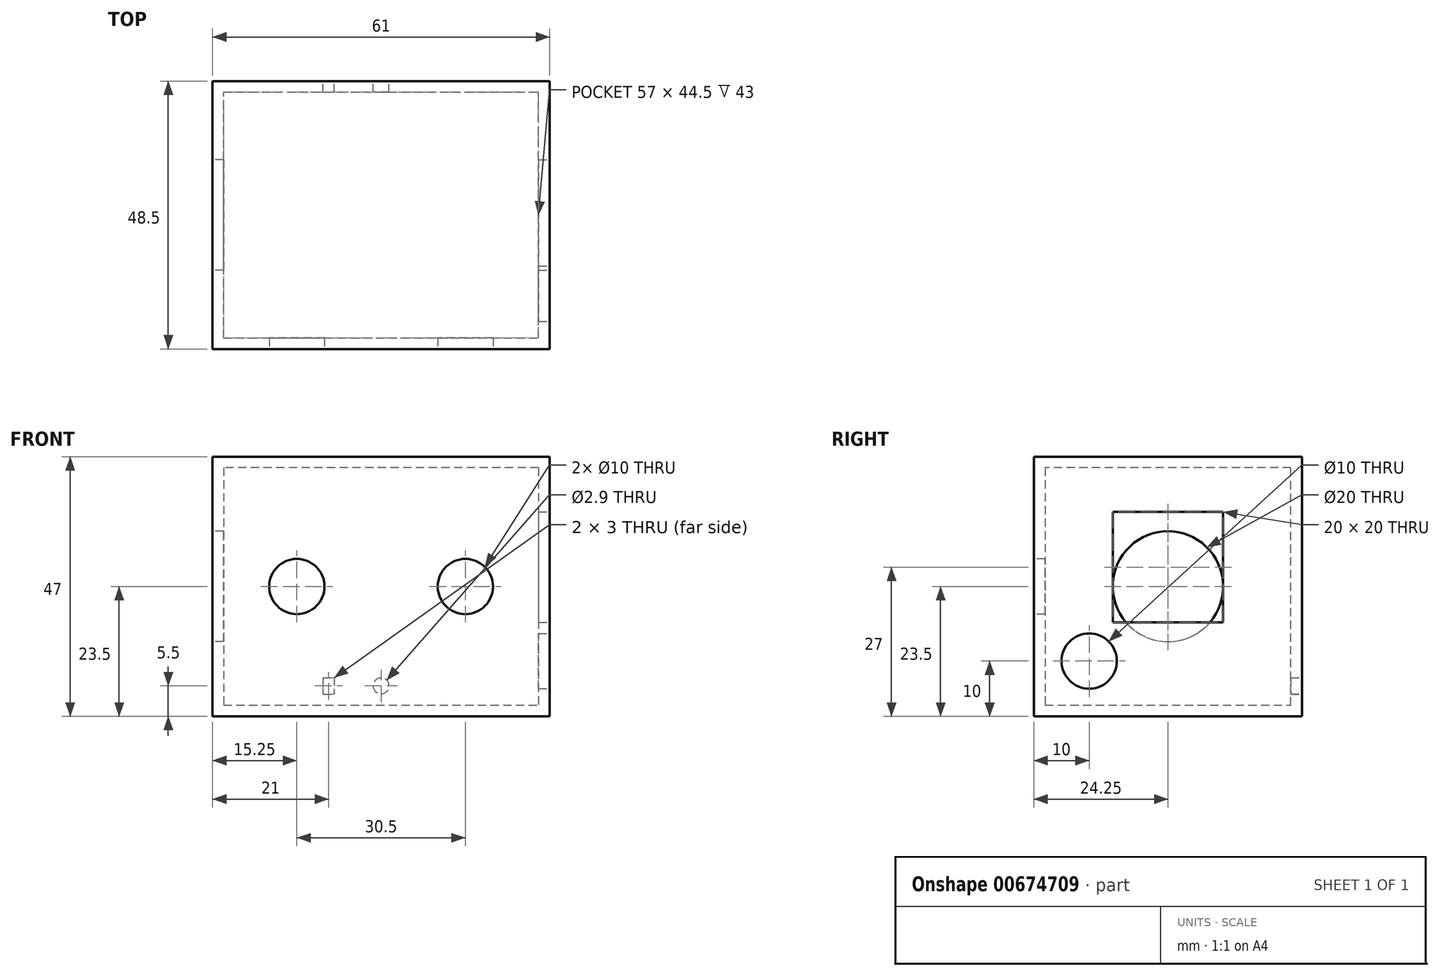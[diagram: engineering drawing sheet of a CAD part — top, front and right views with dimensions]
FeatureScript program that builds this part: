
annotation { "Feature Type Name" : "Feature", "Feature Type Description" : "" }
export const myFeature = defineFeature(function(context is Context, id is Id, definition is map)
    precondition{}
    {
        {
            var Q0;
            Q0=qCreatedBy(makeId("Front.planeOp"),FACE);
            var sketch = newSketch(context, id + "F0", { "sketchPlane" : qUnion([Q0])});
            skLineSegment(sketch, "E0", {"start": v(0, 47) * mm, "end": v(61, 47) * mm});
            skLineSegment(sketch, "E1", {"start": v(61, 47) * mm, "end": v(61, 0) * mm});
            skLineSegment(sketch, "E2", {"start": v(61, 0) * mm, "end": v(0, 0) * mm});
            skLineSegment(sketch, "E3", {"start": v(0, 0) * mm, "end": v(0, 47) * mm});
            skCircle(sketch, "E4", {"center": v(30.5, 5.5) * mm, "radius": 1.45 * mm});
            skLineSegment(sketch, "E5", {"start": v(20, 7) * mm, "end": v(20, 4) * mm});
            skLineSegment(sketch, "E6", {"start": v(20, 5.5) * mm, "end": v(20, 7) * mm});
            skLineSegment(sketch, "E7", {"start": v(20, 7) * mm, "end": v(22, 7) * mm});
            skLineSegment(sketch, "E8", {"start": v(22, 7) * mm, "end": v(22, 5.5) * mm});
            skLineSegment(sketch, "E9.MirrorCS", {"start": v(22, 4) * mm, "end": v(22, 5.5) * mm});
            skLineSegment(sketch, "E10.MirrorCS", {"start": v(20, 4) * mm, "end": v(22, 4) * mm});
            skLineSegment(sketch, "E11.MirrorCS", {"start": v(20, 5.5) * mm, "end": v(20, 4) * mm});
            skPoint(sketch, "E12.start.orphan", {"position": v(30.5, 0) * mm});
            skPoint(sketch, "E13.trimOffspring.end.orphan", {"position": v(30.5, 47) * mm});
            skPoint(sketch, "E13.trimOffspring.start.orphan", {"position": v(30.5, 23.5) * mm});
            skSolve(sketch);
        }
        {
            var Q0;
            Q0=makeQuery(id+"F0.imprint","IMPRINT",FACE,{"disambiguationData":[TD([[makeQuery(id+"F0.imprint","IMPRINT",EDGE,{"derivedFrom":sQuery(id+"F0.wireOp",EDGE,"E0")}),-1.0]])]});
            extrude(context, id + "F1", {"entities" : qUnion([Q0]), "depth" : 2 * mm, "offsetDistance" : 25 * mm});
        }
        {
            var Q0;
            Q0=makeQuery(id+"F1.opExtrude","SWEPT_FACE",FACE,{"disambiguationData":[OSD([sQuery(id+"F0.wireOp",EDGE,"E1")])]});
            cPlane(context, id + "F2", {"entities" : qUnion([Q0]), "cplaneType" : CPlaneType.OFFSET, "offset" : 0 * mm, "width" : 150 * mm, "height" : 150 * mm});
        }
        {
            var Q0;
            Q0=qCreatedBy(id+"F2.planeOp",FACE);
            var sketch = newSketch(context, id + "F3", { "sketchPlane" : qUnion([Q0])});
            skLineSegment(sketch, "E14", {"start": v(0, 0) * mm, "end": v(0, 47) * mm});
            skLineSegment(sketch, "E15", {"start": v(0, 47) * mm, "end": v(-48.5, 47) * mm});
            skLineSegment(sketch, "E16", {"start": v(-48.5, 47) * mm, "end": v(-48.5, 0) * mm});
            skLineSegment(sketch, "E17", {"start": v(-48.5, 0) * mm, "end": v(0, 0) * mm});
            skPoint(sketch, "E18.endSnap0", {"position": v(-48.5, 23.5) * mm});
            skPoint(sketch, "E18.start.orphan", {"position": v(-24.25, 47) * mm});
            skPoint(sketch, "E19.orphan", {"position": v(-36.38, 23.5) * mm});
            skPoint(sketch, "E20.end.orphan", {"position": v(-38.5, 0) * mm});
            skLineSegment(sketch, "E21.top", {"start": v(-24.25, 37) * mm, "end": v(-14.25, 37) * mm});
            skLineSegment(sketch, "E22.top", {"start": v(-24.25, 37) * mm, "end": v(-34.25, 37) * mm});
            skLineSegment(sketch, "E23", {"start": v(-34.25, 37) * mm, "end": v(-34.25, 17) * mm});
            skLineSegment(sketch, "E24", {"start": v(-34.25, 17) * mm, "end": v(-14.25, 17) * mm});
            skLineSegment(sketch, "E25", {"start": v(-14.25, 17) * mm, "end": v(-14.25, 37) * mm});
            skPoint(sketch, "E26", {"position": v(-48.5, 10) * mm});
            skCircle(sketch, "E27", {"center": v(-38.5, 10) * mm, "radius": 5 * mm});
            skSolve(sketch);
        }
        {
            var Q0;
            Q0=makeQuery(id+"F3.imprint","IMPRINT",FACE,{"disambiguationData":[TD([[makeQuery(id+"F3.imprint","IMPRINT",EDGE,{"derivedFrom":sQuery(id+"F3.wireOp",EDGE,"E14")}),1.0]])]});
            extrude(context, id + "F4", {"entities" : qUnion([Q0]), "operationType" : NewBodyOperationType.ADD, "oppositeDirection" : true, "depth" : 2 * mm, "offsetDistance" : 25 * mm});
        }
        {
            var Q0;
            Q0=qCreatedBy(makeId("Right.planeOp"),FACE);
            var sketch = newSketch(context, id + "F5", { "sketchPlane" : qUnion([Q0])});
            skLineSegment(sketch, "E28", {"start": v(0, 0) * mm, "end": v(0, 47) * mm});
            skLineSegment(sketch, "E29", {"start": v(0, 47) * mm, "end": v(-48.5, 47) * mm});
            skLineSegment(sketch, "E30", {"start": v(-48.5, 47) * mm, "end": v(-48.5, 0) * mm});
            skLineSegment(sketch, "E31", {"start": v(-48.5, 0) * mm, "end": v(0, 0) * mm});
            skPoint(sketch, "E32.endSnap0", {"position": v(-48.5, 23.5) * mm});
            skCircle(sketch, "E33", {"center": v(-24.25, 23.5) * mm, "radius": 10 * mm});
            skPoint(sketch, "E34.orphan", {"position": v(-24.25, 47) * mm});
            skSolve(sketch);
        }
        {
            var Q0;
            Q0=makeQuery(id+"F5.imprint","IMPRINT",FACE,{"disambiguationData":[TD([[makeQuery(id+"F5.imprint","IMPRINT",EDGE,{"derivedFrom":sQuery(id+"F5.wireOp",EDGE,"E28")}),1.0]])]});
            extrude(context, id + "F6", {"entities" : qUnion([Q0]), "operationType" : NewBodyOperationType.ADD, "depth" : 2 * mm, "offsetDistance" : 25 * mm});
        }
        {
            var Q0;
            Q0=makeQuery(id+"F4.opExtrude","SWEPT_FACE",FACE,{"disambiguationData":[OSD([sQuery(id+"F3.wireOp",EDGE,"E16")])]});
            cPlane(context, id + "F7", {"entities" : qUnion([Q0]), "cplaneType" : CPlaneType.OFFSET, "offset" : 0 * mm, "width" : 150 * mm, "height" : 150 * mm});
        }
        {
            var Q0;
            Q0=qCreatedBy(id+"F7.planeOp",FACE);
            var sketch = newSketch(context, id + "F8", { "sketchPlane" : qUnion([Q0])});
            skLineSegment(sketch, "E35", {"start": v(0, 0) * mm, "end": v(0, 47) * mm});
            skLineSegment(sketch, "E36", {"start": v(0, 47) * mm, "end": v(61, 47) * mm});
            skLineSegment(sketch, "E37", {"start": v(61, 47) * mm, "end": v(61, 0) * mm});
            skLineSegment(sketch, "E38", {"start": v(61, 0) * mm, "end": v(0, 0) * mm});
            skCircle(sketch, "E39", {"center": v(15.25, 23.5) * mm, "radius": 5 * mm});
            skCircle(sketch, "E40", {"center": v(45.75, 23.5) * mm, "radius": 5 * mm});
            skPoint(sketch, "E41.orphan", {"position": v(30.5, 47) * mm});
            skPoint(sketch, "E42.end.orphan", {"position": v(0, 23.5) * mm});
            skPoint(sketch, "E43.end.orphan", {"position": v(30.5, 0) * mm});
            skPoint(sketch, "E44.orphan", {"position": v(30.5, 23.5) * mm});
            skPoint(sketch, "E45.end.orphan", {"position": v(61, 23.5) * mm});
            skSolve(sketch);
        }
        {
            var Q0;
            Q0=makeQuery(id+"F8.imprint","IMPRINT",FACE,{"disambiguationData":[TD([[makeQuery(id+"F8.imprint","IMPRINT",EDGE,{"derivedFrom":sQuery(id+"F8.wireOp",EDGE,"E35")}),-1.0]])]});
            extrude(context, id + "F9", {"entities" : qUnion([Q0]), "operationType" : NewBodyOperationType.ADD, "oppositeDirection" : true, "depth" : 2 * mm, "offsetDistance" : 25 * mm});
        }
        {
            var Q0;
            Q0=makeQuery(id+"F9.boolean.opBoolean","MERGE",FACE,{"derivedFrom":[makeQuery(id+"F6.boolean.opBoolean","MERGE",FACE,{"derivedFrom":[makeQuery(id+"F4.boolean.opBoolean","MERGE",FACE,{"derivedFrom":[makeQuery(id+"F1.opExtrude","SWEPT_FACE",FACE,{"disambiguationData":[OSD([sQuery(id+"F0.wireOp",EDGE,"E0")])]}),makeQuery(id+"F4.opExtrude","SWEPT_FACE",FACE,{"disambiguationData":[OSD([sQuery(id+"F3.wireOp",EDGE,"E15")])]})]}),makeQuery(id+"F6.opExtrude","SWEPT_FACE",FACE,{"disambiguationData":[OSD([sQuery(id+"F5.wireOp",EDGE,"E29")])]})]}),makeQuery(id+"F9.opExtrude","SWEPT_FACE",FACE,{"disambiguationData":[OSD([sQuery(id+"F8.wireOp",EDGE,"E36")])]})]});
            cPlane(context, id + "F10", {"entities" : qUnion([Q0]), "cplaneType" : CPlaneType.OFFSET, "offset" : 0 * mm, "width" : 150 * mm, "height" : 150 * mm});
        }
        {
            var Q0;
            Q0=qCreatedBy(id+"F10.planeOp",FACE);
            var sketch = newSketch(context, id + "F11", { "sketchPlane" : qUnion([Q0])});
            skLineSegment(sketch, "E46", {"start": v(0, 0) * mm, "end": v(61, 0) * mm});
            skLineSegment(sketch, "E47", {"start": v(61, 0) * mm, "end": v(61, -48.5) * mm});
            skLineSegment(sketch, "E48", {"start": v(61, -48.5) * mm, "end": v(0, -48.5) * mm});
            skLineSegment(sketch, "E49", {"start": v(0, -48.5) * mm, "end": v(0, 0) * mm});
            skSolve(sketch);
        }
        {
            var Q0;
            Q0=makeQuery(id+"F11.imprint","IMPRINT",FACE,{"disambiguationData":[TD([[makeQuery(id+"F11.imprint","IMPRINT",EDGE,{"derivedFrom":sQuery(id+"F11.wireOp",EDGE,"E46")}),-1.0]])]});
            extrude(context, id + "F12", {"entities" : qUnion([Q0]), "operationType" : NewBodyOperationType.ADD, "oppositeDirection" : true, "depth" : 2 * mm, "offsetDistance" : 25 * mm});
        }
        {
            var Q0;
            Q0=makeQuery(id+"F9.boolean.opBoolean","MERGE",FACE,{"derivedFrom":[makeQuery(id+"F6.boolean.opBoolean","MERGE",FACE,{"derivedFrom":[makeQuery(id+"F4.boolean.opBoolean","MERGE",FACE,{"derivedFrom":[makeQuery(id+"F1.opExtrude","SWEPT_FACE",FACE,{"disambiguationData":[OSD([sQuery(id+"F0.wireOp",EDGE,"E2")])]}),makeQuery(id+"F4.opExtrude","SWEPT_FACE",FACE,{"disambiguationData":[OSD([sQuery(id+"F3.wireOp",EDGE,"E17")])]})]}),makeQuery(id+"F6.opExtrude","SWEPT_FACE",FACE,{"disambiguationData":[OSD([sQuery(id+"F5.wireOp",EDGE,"E31")])]})]}),makeQuery(id+"F9.opExtrude","SWEPT_FACE",FACE,{"disambiguationData":[OSD([sQuery(id+"F8.wireOp",EDGE,"E38")])]})]});
            cPlane(context, id + "F13", {"entities" : qUnion([Q0]), "cplaneType" : CPlaneType.OFFSET, "offset" : 0 * mm, "width" : 150 * mm, "height" : 150 * mm});
        }
        {
            var Q0;
            Q0=qCreatedBy(id+"F13.planeOp",FACE);
            var sketch = newSketch(context, id + "F14", { "sketchPlane" : qUnion([Q0])});
            skLineSegment(sketch, "E50", {"start": v(0, 0) * mm, "end": v(0, 48.5) * mm});
            skLineSegment(sketch, "E51", {"start": v(0, 48.5) * mm, "end": v(61, 48.5) * mm});
            skLineSegment(sketch, "E52", {"start": v(61, 48.5) * mm, "end": v(61, 0) * mm});
            skLineSegment(sketch, "E53", {"start": v(61, 0) * mm, "end": v(0, 0) * mm});
            skSolve(sketch);
        }
        {
            var Q0;
            Q0 = qSketchRegion(id + "F14", true);
            extrude(context, id + "F15", {"entities" : qUnion([Q0]), "operationType" : NewBodyOperationType.ADD, "oppositeDirection" : true, "depth" : 2 * mm, "offsetDistance" : 25 * mm});
        }
    });
